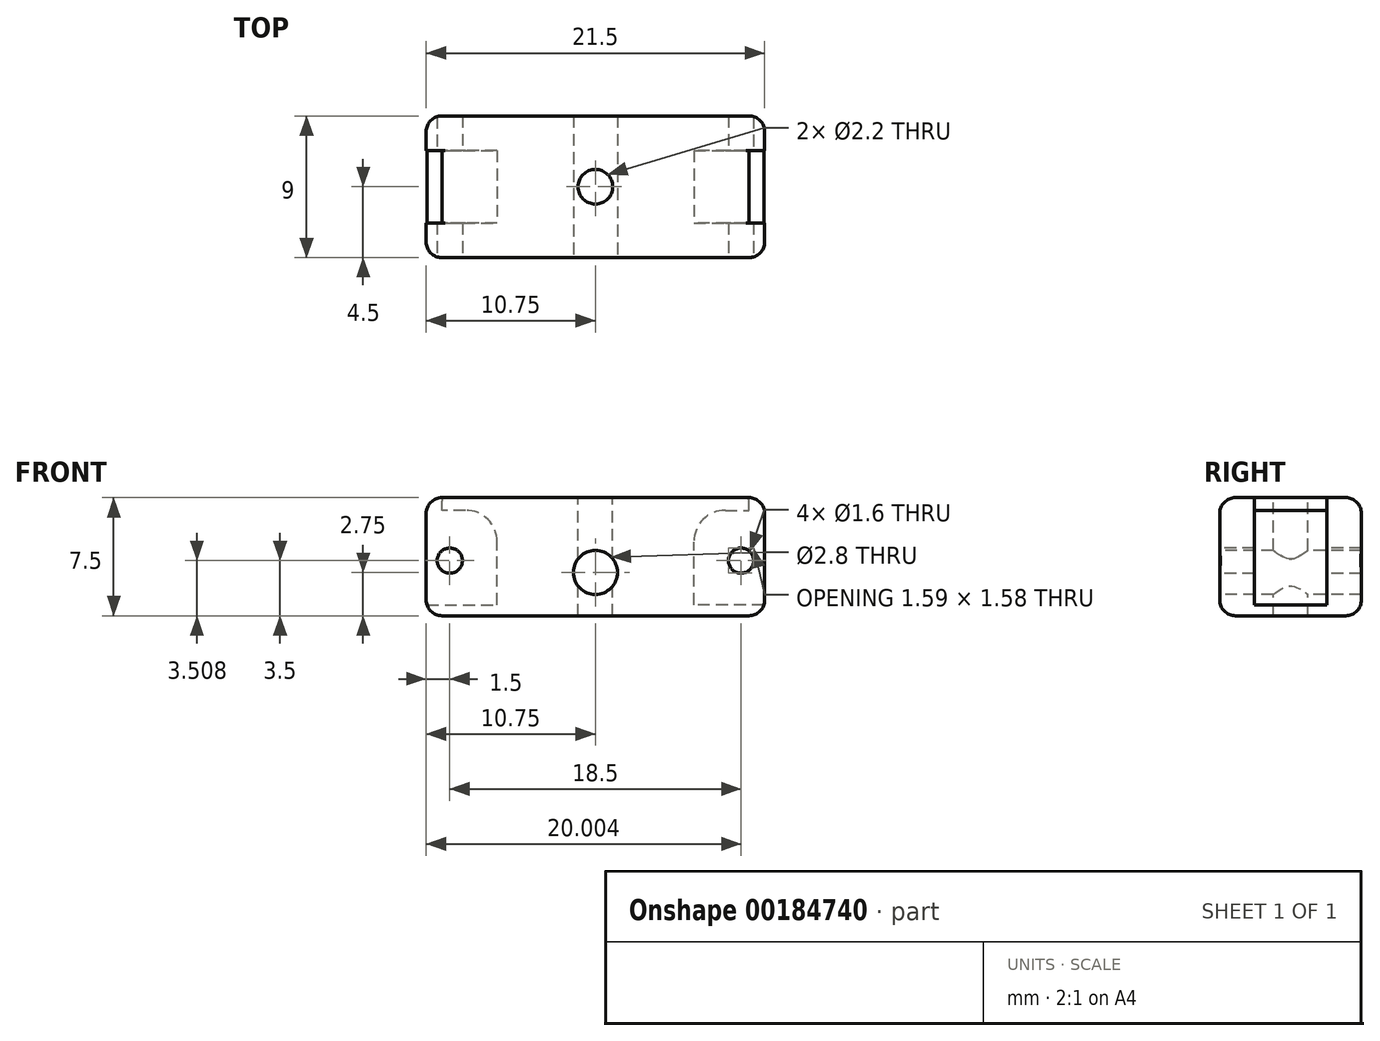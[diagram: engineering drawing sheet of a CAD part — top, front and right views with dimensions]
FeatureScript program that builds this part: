
annotation { "Feature Type Name" : "Feature", "Feature Type Description" : "" }
export const myFeature = defineFeature(function(context is Context, id is Id, definition is map)
    precondition{}
    {
        {
            var Q0;
            Q0=qCreatedBy(makeId("Front.planeOp"),FACE);
            var Q1;
            Q1=qCreatedBy(makeId("Front.planeOp"),FACE);
            var sketch = newSketch(context, id + "F0", { "sketchPlane" : qUnion([Q0, Q1])});
            skLineSegment(sketch, "E0.bottom", {"start": v(-10.75, 4) * mm, "end": v(10.75, 4) * mm});
            skLineSegment(sketch, "E0.top", {"start": v(-10.75, -3.5) * mm, "end": v(10.75, -3.5) * mm});
            skLineSegment(sketch, "E0.left", {"start": v(-10.75, 4) * mm, "end": v(-10.75, -3.5) * mm});
            skLineSegment(sketch, "E0.right", {"start": v(10.75, 4) * mm, "end": v(10.75, -3.5) * mm});
            skCircle(sketch, "E1", {"center": v(-9.25, 0) * mm, "radius": 0.8 * mm});
            skCircle(sketch, "E2.MirrorC", {"center": v(9.25, 0) * mm, "radius": 0.8 * mm});
            skCircle(sketch, "E3", {"center": v(0, -0.75) * mm, "radius": 1.4 * mm});
            skSolve(sketch);
        }
        {
            var Q0;
            Q0=makeQuery(id+"F0.imprint","IMPRINT",FACE,{"disambiguationData":[TD([[makeQuery(id+"F0.imprint","IMPRINT",EDGE,{"derivedFrom":sQuery(id+"F0.wireOp",EDGE,"E0.bottom")}),-1.0]])]});
            extrude(context, id + "F1", {"entities" : qUnion([Q0]), "endBound" : BoundingType.SYMMETRIC, "oppositeDirection" : true, "depth" : 9 * mm});
        }
        {
            var Q0;
            Q0=makeQuery(id+"F1.opExtrude","SWEPT_FACE",FACE,{"disambiguationData":[OSD([sQuery(id+"F0.wireOp",EDGE,"E0.bottom")])]});
            var sketch = newSketch(context, id + "F2", { "sketchPlane" : qUnion([Q0])});
            skCircle(sketch, "E4", {"center": v(0, 0) * mm, "radius": 1.1 * mm});
            skLineSegment(sketch, "E5.bottom", {"start": v(-10.75, -2.3) * mm, "end": v(-6.25, -2.3) * mm});
            skLineSegment(sketch, "E5.top", {"start": v(-10.75, 2.3) * mm, "end": v(-6.25, 2.3) * mm});
            skLineSegment(sketch, "E5.left", {"start": v(-10.75, -2.3) * mm, "end": v(-10.75, 2.3) * mm});
            skLineSegment(sketch, "E5.right", {"start": v(-6.25, -2.3) * mm, "end": v(-6.25, 2.3) * mm});
            skLineSegment(sketch, "E6.MirrorCS", {"start": v(10.75, 2.3) * mm, "end": v(6.25, 2.3) * mm});
            skLineSegment(sketch, "E7.MirrorCS", {"start": v(6.25, -2.3) * mm, "end": v(6.25, 2.3) * mm});
            skLineSegment(sketch, "E8.MirrorCS", {"start": v(10.75, -2.3) * mm, "end": v(6.25, -2.3) * mm});
            skCircle(sketch, "E9", {"center": v(0, 0) * mm, "radius": 3.5 * mm});
            skLineSegment(sketch, "E10", {"start": v(-9.75, -2.3) * mm, "end": v(-9.75, 2.3) * mm});
            skPoint(sketch, "E10.endSnap0", {"position": v(-8.5, 2.3) * mm});
            skLineSegment(sketch, "E11.MirrorCS", {"start": v(9.75, -2.3) * mm, "end": v(9.75, 2.3) * mm});
            skSolve(sketch);
        }
        {
            var Q0;
            Q0=makeQuery(id+"F2.imprint","IMPRINT",FACE,{"disambiguationData":[TD([[makeQuery(id+"F2.imprint","IMPRINT",EDGE,{"derivedFrom":sQuery(id+"F2.wireOp",EDGE,"E4")}),1.0]])]});
            extrude(context, id + "F3", {"entities" : qUnion([Q0]), "operationType" : NewBodyOperationType.REMOVE, "endBound" : BoundingType.THROUGH_ALL, "oppositeDirection" : true, "depth" : 25 * mm});
        }
        {
            var Q0;
            Q0=makeQuery(id+"F2.imprint","IMPRINT",FACE,{"disambiguationData":[TD([[makeQuery(id+"F2.imprint","IMPRINT",EDGE,{"derivedFrom":sQuery(id+"F2.wireOp",EDGE,"E5.bottom")}),1.0]])]});
            var Q1;
            {var subQ0=sQuery(id+"F2.wireOp",EDGE,"E6.MirrorCS");Q1=makeQuery(id+"F2.imprint","IMPRINT",FACE,{"disambiguationData":[TD([[makeQuery(id+"F2.imprint","IMPRINT",EDGE,{"derivedFrom":subQ0}),1.0]])]});}
            extrude(context, id + "F4", {"entities" : qUnion([Q0, Q1]), "operationType" : NewBodyOperationType.REMOVE, "oppositeDirection" : true, "depth" : 6.8 * mm});
        }
        {
            var Q0;
            {var subQ0=sQuery(id+"F2.wireOp",EDGE,"E5.right");Q0=makeQuery(id+"F2.imprint","IMPRINT",FACE,{"disambiguationData":[TD([[makeQuery(id+"F2.imprint","IMPRINT",EDGE,{"derivedFrom":subQ0}),1.0]])]});}
            var Q1;
            {var subQ0=sQuery(id+"F2.wireOp",EDGE,"E7.MirrorCS");Q1=makeQuery(id+"F2.imprint","IMPRINT",FACE,{"disambiguationData":[TD([[makeQuery(id+"F2.imprint","IMPRINT",EDGE,{"derivedFrom":subQ0}),-1.0]])]});}
            var Q2;
            {var subQ10=sQuery(id+"F2.wireOp",EDGE,"E5.right");Q2=makeQuery(id+"F2.imprint","IMPRINT",FACE,{"disambiguationData":[TD([[makeQuery(id+"F2.imprint","IMPRINT",EDGE,{"derivedFrom":subQ10}),-1.0]])]});}
            extrude(context, id + "F5", {"entities" : qUnion([Q0, Q1, Q2]), "operationType" : NewBodyOperationType.ADD, "oppositeDirection" : true, "depth" : 0.8 * mm});
        }
        {
            var Q0;
            Q0=makeQuery(id+"F1.opExtrude","CAP_EDGE",EDGE,{"disambiguationData":[OSD([sQuery(id+"F0.wireOp",EDGE,"E0.top")])],"isStart":true});
            var Q1;
            Q1=makeQuery(id+"F1.opExtrude","CAP_EDGE",EDGE,{"disambiguationData":[OSD([sQuery(id+"F0.wireOp",EDGE,"E0.top")])],"isStart":false});
            var Q2;
            Q2=makeQuery(id+"F1.opExtrude","CAP_EDGE",EDGE,{"disambiguationData":[OSD([sQuery(id+"F0.wireOp",EDGE,"E0.bottom")])],"isStart":true});
            var Q3;
            Q3=makeQuery(id+"F1.opExtrude","CAP_EDGE",EDGE,{"disambiguationData":[OSD([sQuery(id+"F0.wireOp",EDGE,"E0.bottom")])],"isStart":false});
            fillet(context, id + "F6", {"entities" : qUnion([Q0, Q1, Q2, Q3]), "radius" : 1 * mm, "tangentPropagation" : true, "allowEdgeOverflow" : false});
        }
        {
            var Q0;
            {var subQ0=sQuery(id+"F0.wireOp",EDGE,"E0.bottom");var subQ1=sQuery(id+"F0.wireOp",EDGE,"E0.left");Q0=makeQuery(id+"F4.boolean.opBoolean","SPLIT",EDGE,{"disambiguationData":[TD([makeQuery(id+"F4.opExtrude","SWEPT_FACE",FACE,{"disambiguationData":[OSD([sQuery(id+"F2.wireOp",EDGE,"E5.bottom")])]})])],"derivedFrom":makeQuery(id+"F1.opExtrude","SWEPT_EDGE",EDGE,{"disambiguationData":[OSD([subQ0,subQ1])]})});}
            var Q1;
            {var subQ0=sQuery(id+"F0.wireOp",EDGE,"E0.bottom");var subQ1=sQuery(id+"F0.wireOp",EDGE,"E0.right");Q1=makeQuery(id+"F4.boolean.opBoolean","SPLIT",EDGE,{"disambiguationData":[TD([makeQuery(id+"F4.opExtrude","SWEPT_FACE",FACE,{"disambiguationData":[OSD([sQuery(id+"F2.wireOp",EDGE,"E8.MirrorCS")])]})])],"derivedFrom":makeQuery(id+"F1.opExtrude","SWEPT_EDGE",EDGE,{"disambiguationData":[OSD([subQ0,subQ1])]})});}
            fillet(context, id + "F7", {"entities" : qUnion([Q0, Q1]), "radius" : 1 * mm, "tangentPropagation" : true, "allowEdgeOverflow" : false});
        }
        {
            var Q0;
            Q0=makeQuery(id+"F4.boolean.opBoolean","COPY",EDGE,{"derivedFrom":makeQuery(id+"F4.opExtrude","SWEPT_EDGE",EDGE,{"disambiguationData":[OSD([sQuery(id+"F0.wireOp",EDGE,"E0.bottom"),sQuery(id+"F0.wireOp",EDGE,"E0.left"),sQuery(id+"F2.wireOp",EDGE,"E5.bottom"),sQuery(id+"F2.wireOp",EDGE,"E5.left")])]})});
            var Q1;
            Q1=makeQuery(id+"F4.boolean.opBoolean","COPY",EDGE,{"derivedFrom":makeQuery(id+"F4.opExtrude","SWEPT_EDGE",EDGE,{"disambiguationData":[OSD([sQuery(id+"F0.wireOp",EDGE,"E0.bottom"),sQuery(id+"F0.wireOp",EDGE,"E0.left"),sQuery(id+"F2.wireOp",EDGE,"E5.top"),sQuery(id+"F2.wireOp",EDGE,"E5.left")])]})});
            var Q2;
            Q2=makeQuery(id+"F4.boolean.opBoolean","COPY",EDGE,{"derivedFrom":makeQuery(id+"F4.opExtrude","SWEPT_EDGE",EDGE,{"disambiguationData":[OSD([sQuery(id+"F0.wireOp",EDGE,"E0.bottom"),sQuery(id+"F0.wireOp",EDGE,"E0.right"),sQuery(id+"F2.wireOp",EDGE,"E6.MirrorCS")])]})});
            var Q3;
            Q3=makeQuery(id+"F4.boolean.opBoolean","COPY",EDGE,{"derivedFrom":makeQuery(id+"F4.opExtrude","SWEPT_EDGE",EDGE,{"disambiguationData":[OSD([sQuery(id+"F0.wireOp",EDGE,"E0.bottom"),sQuery(id+"F0.wireOp",EDGE,"E0.right"),sQuery(id+"F2.wireOp",EDGE,"E8.MirrorCS")])]})});
            var Q4;
            Q4=makeQuery(id+"F5.opExtrude","CAP_EDGE",EDGE,{"disambiguationData":[OSD([sQuery(id+"F2.wireOp",EDGE,"E10")])],"isStart":true});
            var Q5;
            Q5=makeQuery(id+"F5.opExtrude","CAP_EDGE",EDGE,{"disambiguationData":[OSD([sQuery(id+"F2.wireOp",EDGE,"E11.MirrorCS")])],"isStart":true});
            fillet(context, id + "F8", {"entities" : qUnion([Q0, Q1, Q2, Q3, Q4, Q5]), "radius" : 0.2 * mm, "tangentPropagation" : true, "allowEdgeOverflow" : false});
        }
        {
            var Q0;
            Q0=makeQuery(id+"F5.boolean.opBoolean","INTERSECT",EDGE,{"derivedFrom":[makeQuery(id+"F4.boolean.opBoolean","COPY",FACE,{"derivedFrom":makeQuery(id+"F4.opExtrude","SWEPT_FACE",FACE,{"disambiguationData":[OSD([sQuery(id+"F2.wireOp",EDGE,"E7.MirrorCS")])]})}),makeQuery(id+"F5.opExtrude","CAP_FACE",FACE,{"disambiguationData":[OSD([sQuery(id+"F0.wireOp",EDGE,"E0.bottom"),sQuery(id+"F0.wireOp",EDGE,"E0.left"),sQuery(id+"F0.wireOp",EDGE,"E0.right"),sQuery(id+"F2.wireOp",EDGE,"E5.bottom"),sQuery(id+"F2.wireOp",EDGE,"E5.top"),sQuery(id+"F2.wireOp",EDGE,"E6.MirrorCS"),sQuery(id+"F2.wireOp",EDGE,"E8.MirrorCS"),sQuery(id+"F2.wireOp",EDGE,"E9"),sQuery(id+"F2.wireOp",EDGE,"E10"),sQuery(id+"F2.wireOp",EDGE,"E11.MirrorCS")])],"isStart":false})]});
            var Q1;
            Q1=makeQuery(id+"F5.boolean.opBoolean","INTERSECT",EDGE,{"derivedFrom":[makeQuery(id+"F4.boolean.opBoolean","COPY",FACE,{"derivedFrom":makeQuery(id+"F4.opExtrude","SWEPT_FACE",FACE,{"disambiguationData":[OSD([sQuery(id+"F2.wireOp",EDGE,"E5.right")])]})}),makeQuery(id+"F5.opExtrude","CAP_FACE",FACE,{"disambiguationData":[OSD([sQuery(id+"F0.wireOp",EDGE,"E0.bottom"),sQuery(id+"F0.wireOp",EDGE,"E0.left"),sQuery(id+"F0.wireOp",EDGE,"E0.right"),sQuery(id+"F2.wireOp",EDGE,"E5.bottom"),sQuery(id+"F2.wireOp",EDGE,"E5.top"),sQuery(id+"F2.wireOp",EDGE,"E6.MirrorCS"),sQuery(id+"F2.wireOp",EDGE,"E8.MirrorCS"),sQuery(id+"F2.wireOp",EDGE,"E9"),sQuery(id+"F2.wireOp",EDGE,"E10"),sQuery(id+"F2.wireOp",EDGE,"E11.MirrorCS")])],"isStart":false})]});
            fillet(context, id + "F9", {"entities" : qUnion([Q0, Q1]), "radius" : 2 * mm, "tangentPropagation" : true, "allowEdgeOverflow" : false});
        }
    });
